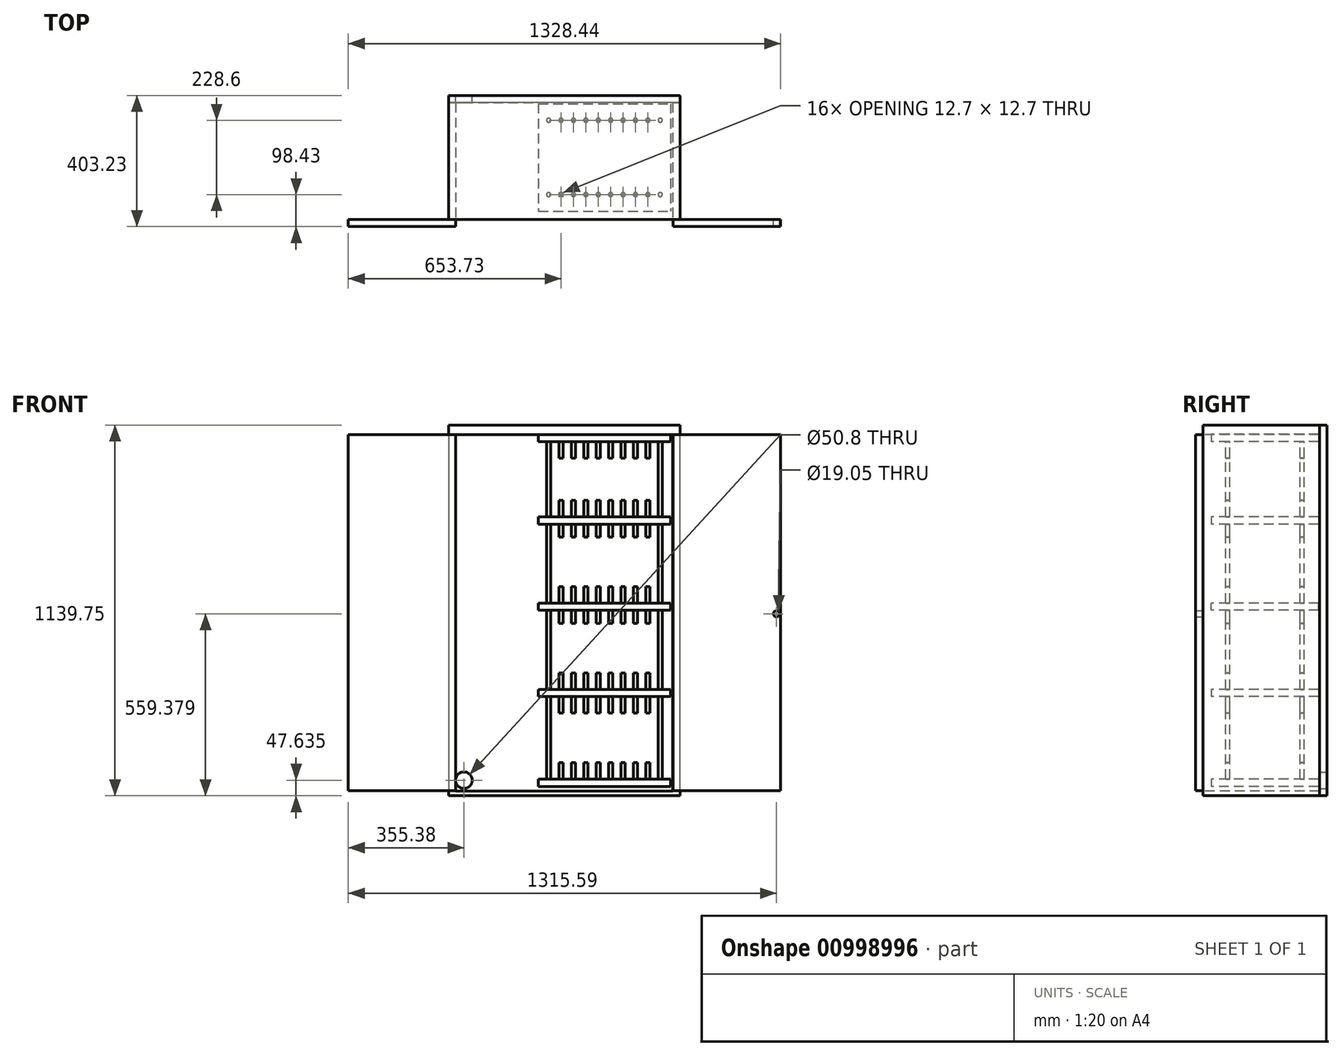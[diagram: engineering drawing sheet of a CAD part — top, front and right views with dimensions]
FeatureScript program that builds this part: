
annotation { "Feature Type Name" : "Feature", "Feature Type Description" : "" }
export const myFeature = defineFeature(function(context is Context, id is Id, definition is map)
    precondition{}
    {
        {
            var Q0;
            Q0=qCreatedBy(makeId("Front.planeOp"),FACE);
            var sketch = newSketch(context, id + "F0", { "sketchPlane" : qUnion([Q0])});
            skLineSegment(sketch, "E0.bottom", {"start": v(-203.2, -11.11) * mm, "end": v(203.2, -11.11) * mm});
            skLineSegment(sketch, "E0.top", {"start": v(-203.2, 11.11) * mm, "end": v(203.2, 11.11) * mm});
            skLineSegment(sketch, "E0.left", {"start": v(-203.2, -11.11) * mm, "end": v(-203.2, 11.11) * mm});
            skLineSegment(sketch, "E0.right", {"start": v(203.2, -11.11) * mm, "end": v(203.2, 11.11) * mm});
            skPoint(sketch, "E0.middle", {"position": v(0, 0) * mm});
            skLineSegment(sketch, "E1.bottom", {"start": v(-203.2, 276.22) * mm, "end": v(203.2, 276.22) * mm});
            skLineSegment(sketch, "E1.top", {"start": v(-203.2, 254) * mm, "end": v(203.2, 254) * mm});
            skLineSegment(sketch, "E1.left", {"start": v(-203.2, 276.22) * mm, "end": v(-203.2, 254) * mm});
            skLineSegment(sketch, "E1.right", {"start": v(203.2, 276.22) * mm, "end": v(203.2, 254) * mm});
            skPoint(sketch, "E1.middle", {"position": v(0, 265.11) * mm});
            skLineSegment(sketch, "E2.bottom", {"start": v(-203.2, 530.22) * mm, "end": v(203.2, 530.22) * mm});
            skLineSegment(sketch, "E2.top", {"start": v(-203.2, 508) * mm, "end": v(203.2, 508) * mm});
            skLineSegment(sketch, "E2.left", {"start": v(-203.2, 530.22) * mm, "end": v(-203.2, 508) * mm});
            skLineSegment(sketch, "E2.right", {"start": v(203.2, 530.22) * mm, "end": v(203.2, 508) * mm});
            skPoint(sketch, "E2.middle", {"position": v(0, 519.11) * mm});
            skLineSegment(sketch, "E3.bottom", {"start": v(-203.2, -254) * mm, "end": v(203.2, -254) * mm});
            skLineSegment(sketch, "E3.top", {"start": v(-203.2, -276.22) * mm, "end": v(203.2, -276.22) * mm});
            skLineSegment(sketch, "E3.left", {"start": v(-203.2, -254) * mm, "end": v(-203.2, -276.22) * mm});
            skLineSegment(sketch, "E3.right", {"start": v(203.2, -254) * mm, "end": v(203.2, -276.22) * mm});
            skPoint(sketch, "E3.middle", {"position": v(0, -265.11) * mm});
            skLineSegment(sketch, "E4.bottom", {"start": v(-203.2, -530.24) * mm, "end": v(203.2, -530.24) * mm});
            skLineSegment(sketch, "E4.top", {"start": v(-203.2, -552.46) * mm, "end": v(203.2, -552.46) * mm});
            skLineSegment(sketch, "E4.left", {"start": v(-203.2, -530.24) * mm, "end": v(-203.2, -552.46) * mm});
            skLineSegment(sketch, "E4.right", {"start": v(203.2, -530.24) * mm, "end": v(203.2, -552.46) * mm});
            skPoint(sketch, "E4.middle", {"position": v(0, -541.35) * mm});
            skLineSegment(sketch, "E5.top", {"start": v(-165.1, 327.02) * mm, "end": v(165.1, 327.02) * mm});
            skLineSegment(sketch, "E5.left", {"start": v(-165.1, 457.2) * mm, "end": v(-165.1, 327.02) * mm});
            skLineSegment(sketch, "E5.right", {"start": v(165.1, 457.2) * mm, "end": v(165.1, 327.02) * mm});
            skLineSegment(sketch, "E6", {"start": v(165.1, 457.2) * mm, "end": v(-165.1, 457.2) * mm});
            skPoint(sketch, "E6.startSnap0", {"position": v(165.1, 403.22) * mm});
            skLineSegment(sketch, "E7.bottom", {"start": v(-165.1, 214.31) * mm, "end": v(165.1, 214.31) * mm});
            skLineSegment(sketch, "E7.top", {"start": v(-165.1, 61.91) * mm, "end": v(165.1, 61.91) * mm});
            skLineSegment(sketch, "E7.left", {"start": v(-165.1, 214.31) * mm, "end": v(-165.1, 61.91) * mm});
            skLineSegment(sketch, "E7.right", {"start": v(165.1, 214.31) * mm, "end": v(165.1, 61.91) * mm});
            skPoint(sketch, "E7.middle", {"position": v(0, 138.11) * mm});
            skLineSegment(sketch, "E8.bottom", {"start": v(-165.1, -50.8) * mm, "end": v(165.1, -50.8) * mm});
            skLineSegment(sketch, "E8.top", {"start": v(-165.1, -203.2) * mm, "end": v(165.1, -203.2) * mm});
            skLineSegment(sketch, "E8.left", {"start": v(-165.1, -50.8) * mm, "end": v(-165.1, -203.2) * mm});
            skLineSegment(sketch, "E8.right", {"start": v(165.1, -50.8) * mm, "end": v(165.1, -203.2) * mm});
            skPoint(sketch, "E8.middle", {"position": v(0, -127) * mm});
            skLineSegment(sketch, "E9.bottom", {"start": v(-165.1, -327.04) * mm, "end": v(165.1, -327.04) * mm});
            skLineSegment(sketch, "E9.top", {"start": v(-165.1, -479.44) * mm, "end": v(165.1, -479.44) * mm});
            skLineSegment(sketch, "E9.left", {"start": v(-165.1, -327.04) * mm, "end": v(-165.1, -479.44) * mm});
            skLineSegment(sketch, "E9.right", {"start": v(165.1, -327.04) * mm, "end": v(165.1, -479.44) * mm});
            skPoint(sketch, "E9.middle", {"position": v(0, -403.24) * mm});
            skSolve(sketch);
        }
        {
            var Q0;
            Q0=makeQuery(id+"F0.imprint","IMPRINT",FACE,{"disambiguationData":[TD([[makeQuery(id+"F0.imprint","IMPRINT",EDGE,{"derivedFrom":sQuery(id+"F0.wireOp",EDGE,"E3.bottom")}),-1.0]])]});
            var Q1;
            Q1=makeQuery(id+"F0.imprint","IMPRINT",FACE,{"disambiguationData":[TD([[makeQuery(id+"F0.imprint","IMPRINT",EDGE,{"derivedFrom":sQuery(id+"F0.wireOp",EDGE,"E0.bottom")}),1.0]])]});
            var Q2;
            Q2=makeQuery(id+"F0.imprint","IMPRINT",FACE,{"disambiguationData":[TD([[makeQuery(id+"F0.imprint","IMPRINT",EDGE,{"derivedFrom":sQuery(id+"F0.wireOp",EDGE,"E1.bottom")}),-1.0]])]});
            var Q3;
            Q3=makeQuery(id+"F0.imprint","IMPRINT",FACE,{"disambiguationData":[TD([[makeQuery(id+"F0.imprint","IMPRINT",EDGE,{"derivedFrom":sQuery(id+"F0.wireOp",EDGE,"E2.bottom")}),-1.0]])]});
            var Q4;
            Q4=makeQuery(id+"F0.imprint","IMPRINT",FACE,{"disambiguationData":[TD([[makeQuery(id+"F0.imprint","IMPRINT",EDGE,{"derivedFrom":sQuery(id+"F0.wireOp",EDGE,"E4.bottom")}),-1.0]])]});
            extrude(context, id + "F1", {"entities" : qUnion([Q0, Q1, Q2, Q3, Q4]), "oppositeDirection" : true, "depth" : 330.2 * mm, "offsetDistance" : 25.4 * mm});
        }
        {
            var Q0;
            Q0=makeQuery(id+"F1.opExtrude","SWEPT_FACE",FACE,{"disambiguationData":[OSD([sQuery(id+"F0.wireOp",EDGE,"E0.top")])]});
            cPlane(context, id + "F2", {"entities" : qUnion([Q0]), "cplaneType" : CPlaneType.OFFSET, "offset" : 0 * mm, "width" : 152.4 * mm, "height" : 152.4 * mm});
        }
        {
            var Q0;
            Q0=qCreatedBy(id+"F2.planeOp",FACE);
            var sketch = newSketch(context, id + "F3", { "sketchPlane" : qUnion([Q0])});
            skLineSegment(sketch, "E10.bottom", {"start": v(-203.2, 330.2) * mm, "end": v(203.2, 330.2) * mm, "construction": true});
            skLineSegment(sketch, "E10.top", {"start": v(-203.2, 0) * mm, "end": v(203.2, 0) * mm, "construction": true});
            skLineSegment(sketch, "E10.left", {"start": v(-203.2, 330.2) * mm, "end": v(-203.2, 0) * mm, "construction": true});
            skLineSegment(sketch, "E10.right", {"start": v(203.2, 330.2) * mm, "end": v(203.2, 0) * mm, "construction": true});
            skPoint(sketch, "E11", {"position": v(171.45, 279.4) * mm});
            skPoint(sketch, "E12", {"position": v(171.45, 50.8) * mm});
            skCircle(sketch, "E13", {"center": v(171.45, 279.4) * mm, "radius": 6.35 * mm});
            skCircle(sketch, "E14", {"center": v(171.45, 50.8) * mm, "radius": 6.35 * mm});
            skCircle(sketch, "E15.1.0.0", {"center": v(133.35, 279.4) * mm, "radius": 6.35 * mm});
            skCircle(sketch, "E15.1.0.1", {"center": v(133.35, 50.8) * mm, "radius": 6.35 * mm});
            skCircle(sketch, "E15.2.0.0", {"center": v(95.25, 279.4) * mm, "radius": 6.35 * mm});
            skCircle(sketch, "E15.2.0.1", {"center": v(95.25, 50.8) * mm, "radius": 6.35 * mm});
            skCircle(sketch, "E15.3.0.0", {"center": v(57.15, 279.4) * mm, "radius": 6.35 * mm});
            skCircle(sketch, "E15.3.0.1", {"center": v(57.15, 50.8) * mm, "radius": 6.35 * mm});
            skCircle(sketch, "E15.4.0.0", {"center": v(19.05, 279.4) * mm, "radius": 6.35 * mm});
            skCircle(sketch, "E15.4.0.1", {"center": v(19.05, 50.8) * mm, "radius": 6.35 * mm});
            skCircle(sketch, "E15.5.0.0", {"center": v(-19.05, 279.4) * mm, "radius": 6.35 * mm});
            skCircle(sketch, "E15.5.0.1", {"center": v(-19.05, 50.8) * mm, "radius": 6.35 * mm});
            skCircle(sketch, "E15.6.0.0", {"center": v(-57.15, 279.4) * mm, "radius": 6.35 * mm});
            skCircle(sketch, "E15.6.0.1", {"center": v(-57.15, 50.8) * mm, "radius": 6.35 * mm});
            skCircle(sketch, "E15.7.0.0", {"center": v(-95.25, 279.4) * mm, "radius": 6.35 * mm});
            skCircle(sketch, "E15.7.0.1", {"center": v(-95.25, 50.8) * mm, "radius": 6.35 * mm});
            skCircle(sketch, "E15.8.0.0", {"center": v(-133.35, 279.4) * mm, "radius": 6.35 * mm});
            skCircle(sketch, "E15.8.0.1", {"center": v(-133.35, 50.8) * mm, "radius": 6.35 * mm});
            skCircle(sketch, "E15.9.0.0", {"center": v(-171.45, 279.4) * mm, "radius": 6.35 * mm});
            skCircle(sketch, "E15.9.0.1", {"center": v(-171.45, 50.8) * mm, "radius": 6.35 * mm});
            skSolve(sketch);
        }
        {
            var Q0;
            Q0 = qSketchRegion(id + "F3", true);
            extrude(context, id + "F4", {"entities" : qUnion([Q0]), "operationType" : NewBodyOperationType.ADD, "oppositeDirection" : true, "depth" : 563.58 * mm, "offsetDistance" : 25.4 * mm, "hasSecondDirection" : true, "secondDirectionOppositeDirection" : false, "secondDirectionDepth" : 519.13 * mm});
        }
        {
            var Q0;
            Q0=makeQuery(id+"F0.imprint","IMPRINT",FACE,{"disambiguationData":[TD([[makeQuery(id+"F0.imprint","IMPRINT",EDGE,{"derivedFrom":sQuery(id+"F0.wireOp",EDGE,"E5.top")}),1.0]])]});
            var Q1;
            Q1=makeQuery(id+"F0.imprint","IMPRINT",FACE,{"disambiguationData":[TD([[makeQuery(id+"F0.imprint","IMPRINT",EDGE,{"derivedFrom":sQuery(id+"F0.wireOp",EDGE,"E7.bottom")}),-1.0]])]});
            var Q2;
            Q2=makeQuery(id+"F0.imprint","IMPRINT",FACE,{"disambiguationData":[TD([[makeQuery(id+"F0.imprint","IMPRINT",EDGE,{"derivedFrom":sQuery(id+"F0.wireOp",EDGE,"E8.bottom")}),-1.0]])]});
            var Q3;
            Q3=makeQuery(id+"F0.imprint","IMPRINT",FACE,{"disambiguationData":[TD([[makeQuery(id+"F0.imprint","IMPRINT",EDGE,{"derivedFrom":sQuery(id+"F0.wireOp",EDGE,"E9.bottom")}),-1.0]])]});
            extrude(context, id + "F5", {"entities" : qUnion([Q0, Q1, Q2, Q3]), "operationType" : NewBodyOperationType.REMOVE, "oppositeDirection" : true, "depth" : 304.8 * mm, "hasOffset" : true, "offsetDistance" : 25.4 * mm, "offsetOppositeDirection" : true});
        }
        {
            var Q0;
            Q0=qCreatedBy(makeId("Front.planeOp"),FACE);
            var sketch = newSketch(context, id + "F6", { "sketchPlane" : qUnion([Q0])});
            skLineSegment(sketch, "E16.bottom", {"start": v(209.63, -566.44) * mm, "end": v(-457.12, -566.44) * mm});
            skLineSegment(sketch, "E16.top", {"start": v(209.63, 528.84) * mm, "end": v(-457.12, 528.84) * mm});
            skLineSegment(sketch, "E17.0", {"start": v(231.86, 558.64) * mm, "end": v(-479.34, 558.64) * mm});
            skLineSegment(sketch, "E18.0", {"start": v(231.86, -581.08) * mm, "end": v(-479.34, -581.08) * mm});
            skLineSegment(sketch, "E19", {"start": v(-479.34, 558.64) * mm, "end": v(-479.34, -581.08) * mm});
            skLineSegment(sketch, "E20", {"start": v(-457.12, 528.84) * mm, "end": v(-457.12, -566.44) * mm});
            skLineSegment(sketch, "E21", {"start": v(209.63, 528.84) * mm, "end": v(209.63, -566.44) * mm});
            skLineSegment(sketch, "E22", {"start": v(231.86, -581.08) * mm, "end": v(231.86, 558.64) * mm});
            skSolve(sketch);
        }
        {
            var Q0;
            Q0=makeQuery(id+"F6.imprint","IMPRINT",FACE,{"disambiguationData":[TD([[makeQuery(id+"F6.imprint","IMPRINT",EDGE,{"derivedFrom":sQuery(id+"F6.wireOp",EDGE,"E16.bottom")}),1.0]])]});
            extrude(context, id + "F7", {"entities" : qUnion([Q0]), "oppositeDirection" : true, "depth" : 355.6 * mm, "offsetDistance" : 25.4 * mm, "hasSecondDirection" : true, "secondDirectionOppositeDirection" : false, "secondDirectionDepth" : 25.4 * mm});
        }
        {
            var Q0;
            Q0=makeQuery(id+"F7.opExtrude","CAP_FACE",FACE,{"disambiguationData":[OSD([sQuery(id+"F6.wireOp",EDGE,"E16.bottom"),sQuery(id+"F6.wireOp",EDGE,"E16.top"),sQuery(id+"F6.wireOp",EDGE,"E16.left"),sQuery(id+"F6.wireOp",EDGE,"E16.right"),sQuery(id+"F6.wireOp",EDGE,"E17.0"),sQuery(id+"F6.wireOp",EDGE,"fd27da03-2fb2-4175-96d7-ff5d5455aa17.0"),sQuery(id+"F6.wireOp",EDGE,"2eda592c-bfc0-441b-a2c1-ea656dcc7ac0.0"),sQuery(id+"F6.wireOp",EDGE,"E18.0")])],"isStart":false});
            cPlane(context, id + "F8", {"entities" : qUnion([Q0]), "cplaneType" : CPlaneType.OFFSET, "offset" : 0 * mm, "width" : 152.4 * mm, "height" : 152.4 * mm});
        }
        {
            var Q0;
            Q0=qCreatedBy(id+"F8.planeOp",FACE);
            var sketch = newSketch(context, id + "F9", { "sketchPlane" : qUnion([Q0])});
            skLineSegment(sketch, "E23.0", {"start": v(479.33, 558.62) * mm, "end": v(-231.87, 558.62) * mm});
            skLineSegment(sketch, "E24.0", {"start": v(-231.87, -581.1) * mm, "end": v(-231.87, 558.62) * mm});
            skLineSegment(sketch, "E25.0", {"start": v(479.33, -581.1) * mm, "end": v(479.33, 558.62) * mm});
            skLineSegment(sketch, "E26.0", {"start": v(479.33, -581.1) * mm, "end": v(-231.87, -581.1) * mm});
            skPoint(sketch, "E27", {"position": v(457.2, 536.49) * mm});
            skPoint(sketch, "E28", {"position": v(479.33, 558.62) * mm});
            skPoint(sketch, "E29", {"position": v(457.1, -558.88) * mm});
            skLineSegment(sketch, "E30", {"start": v(457.1, -508.08) * mm, "end": v(406.3, -558.88) * mm, "construction": true});
            skLineSegment(sketch, "E31", {"start": v(447.12, -554.36) * mm, "end": v(457.1, -558.88) * mm, "construction": true});
            skLineSegment(sketch, "E32", {"start": v(406.3, -508.08) * mm, "end": v(457.1, -558.88) * mm, "construction": true});
            skCircle(sketch, "E33", {"center": v(431.7, -533.48) * mm, "radius": 25.4 * mm});
            skSolve(sketch);
        }
        {
            var Q0;
            Q0=makeQuery(id+"F9.imprint","IMPRINT",FACE,{"disambiguationData":[TD([[makeQuery(id+"F9.imprint","IMPRINT",EDGE,{"derivedFrom":sQuery(id+"F9.wireOp",EDGE,"E23.0")}),1.0]])]});
            extrude(context, id + "F10", {"entities" : qUnion([Q0]), "operationType" : NewBodyOperationType.ADD, "oppositeDirection" : true, "depth" : 22.22 * mm, "offsetDistance" : 25.4 * mm});
        }
        {
            var Q0;
            Q0=makeQuery(id+"F9.imprint","IMPRINT",FACE,{"disambiguationData":[TD([[makeQuery(id+"F9.imprint","IMPRINT",EDGE,{"derivedFrom":sQuery(id+"F9.wireOp",EDGE,"E33")}),1.0]])]});
            extrude(context, id + "F11", {"entities" : qUnion([Q0]), "operationType" : NewBodyOperationType.REMOVE, "oppositeDirection" : true, "depth" : 25.4 * mm, "offsetDistance" : 25.4 * mm});
        }
        {
            var Q0;
            Q0=makeQuery(id+"F7.opExtrude","CAP_FACE",FACE,{"disambiguationData":[OSD([sQuery(id+"F6.wireOp",EDGE,"E16.bottom"),sQuery(id+"F6.wireOp",EDGE,"E16.top"),sQuery(id+"F6.wireOp",EDGE,"E17.0"),sQuery(id+"F6.wireOp",EDGE,"E18.0"),sQuery(id+"F6.wireOp",EDGE,"E19"),sQuery(id+"F6.wireOp",EDGE,"E20"),sQuery(id+"F6.wireOp",EDGE,"E21"),sQuery(id+"F6.wireOp",EDGE,"E22")])],"isStart":true});
            cPlane(context, id + "F12", {"entities" : qUnion([Q0]), "cplaneType" : CPlaneType.OFFSET, "offset" : 0 * mm, "width" : 152.4 * mm, "height" : 152.4 * mm});
        }
        {
            var Q0;
            Q0=qCreatedBy(id+"F12.planeOp",FACE);
            var sketch = newSketch(context, id + "F13", { "sketchPlane" : qUnion([Q0])});
            skLineSegment(sketch, "E34", {"start": v(-477.44, -582.98) * mm, "end": v(231.73, 558.77) * mm, "construction": true});
            skLineSegment(sketch, "E35", {"start": v(-477.44, 558.77) * mm, "end": v(231.73, -582.98) * mm, "construction": true});
            skPoint(sketch, "E36", {"position": v(-122.86, -12.1) * mm});
            skLineSegment(sketch, "E37", {"start": v(-122.86, -676.95) * mm, "end": v(-122.86, 636.78) * mm, "construction": true});
            skPoint(sketch, "E38", {"position": v(-456.88, 528.8) * mm});
            skLineSegment(sketch, "E39", {"start": v(-456.88, 528.8) * mm, "end": v(-787.08, 528.8) * mm});
            skPoint(sketch, "E40", {"position": v(-456.52, -566.3) * mm});
            skLineSegment(sketch, "E41", {"start": v(-456.52, -566.3) * mm, "end": v(-786.72, -566.3) * mm});
            skLineSegment(sketch, "E42", {"start": v(-786.72, -566.3) * mm, "end": v(-787.08, 528.8) * mm});
            skLineSegment(sketch, "E43.MirrorCS", {"start": v(211.16, 528.8) * mm, "end": v(210.81, -566.3) * mm});
            skLineSegment(sketch, "E44.MirrorCS", {"start": v(211.16, 528.8) * mm, "end": v(541.36, 528.8) * mm});
            skLineSegment(sketch, "E45.MirrorCS", {"start": v(541.01, -566.3) * mm, "end": v(541.36, 528.8) * mm});
            skLineSegment(sketch, "E46.MirrorCS", {"start": v(210.81, -566.3) * mm, "end": v(541.01, -566.3) * mm});
            skCircle(sketch, "E47", {"center": v(528.51, -21.73) * mm, "radius": 9.53 * mm});
            skLineSegment(sketch, "E48", {"start": v(-354.9, -12.1) * mm, "end": v(258.44, -12.1) * mm, "construction": true});
            skLineSegment(sketch, "E49", {"start": v(-456.88, 528.8) * mm, "end": v(-456.52, -566.3) * mm});
            skSolve(sketch);
        }
        {
            var Q0;
            Q0=makeQuery(id+"F13.imprint","IMPRINT",FACE,{"disambiguationData":[TD([[makeQuery(id+"F13.imprint","IMPRINT",EDGE,{"derivedFrom":sQuery(id+"F13.wireOp",EDGE,"E39")}),1.0]])]});
            var Q1;
            Q1=makeQuery(id+"F13.imprint","IMPRINT",FACE,{"disambiguationData":[TD([[makeQuery(id+"F13.imprint","IMPRINT",EDGE,{"derivedFrom":sQuery(id+"F13.wireOp",EDGE,"E43.MirrorCS")}),1.0]])]});
            var Q2;
            {var subQ5=sQuery(id+"F13.wireOp",EDGE,"945d7d3f-2e24-4aa4-a8fb-3bcfb2968ccc0.MirrorCS");Q2=makeQuery(id+"F13.imprint","IMPRINT",FACE,{"disambiguationData":[TD([[makeQuery(id+"F13.imprint","IMPRINT",EDGE,{"derivedFrom":subQ5}),1.0]])]});}
            var Q3;
            Q3=makeQuery(id+"F13.imprint","IMPRINT",FACE,{"disambiguationData":[TD([[makeQuery(id+"F13.imprint","IMPRINT",EDGE,{"derivedFrom":sQuery(id+"F13.wireOp",EDGE,"PqKMKNCi-Sgya-wTwO-OgJu-uYzNobhRPgVU.bottom")}),1.0]])]});
            extrude(context, id + "F14", {"entities" : qUnion([Q0, Q1, Q2, Q3]), "operationType" : NewBodyOperationType.ADD, "depth" : 22.22 * mm, "offsetDistance" : 25.4 * mm});
        }
    });
